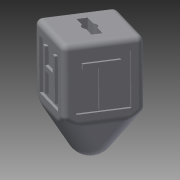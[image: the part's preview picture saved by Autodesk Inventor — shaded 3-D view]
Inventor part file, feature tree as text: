
AUTODESK INVENTOR PART (.ipt)
format: ipt  version: 2015 (Build 190159000, 159)  size: 379,904 bytes
history: native  units: in
note: dims shown in document units (in); Inventor stores cm internally (conversion verified against a paired STEP export)
features: extrude x13, sketch x13, projected_geometry x8, fillet x4
ambient origin geometry x8: Origin, YZ Plane, XZ Plane, XY Plane, X Axis, Y Axis, Z Axis, Center Point
bodies: Solid1 (feature_tree)
feature tree (38):
  extrude  "Extrusion1"  Depth=1.5in
  extrude  "Extrusion2"  Depth=0.25in
  extrude  "Extrusion3"  Depth=0.0625in
  fillet  "Fillet1"  Radius=0.4375in
  fillet  "Fillet2"  Radius=0.125in
  fillet  "Fillet3"  Radius=0.125in
  fillet  "Fillet4"  Radius=0.0625in
  extrude  "Extrusion4"  Depth=0.125in
  extrude  "Extrusion5"  Depth=0.125in
  extrude  "Extrusion6"  Depth=0.0625in TaperAngle=0.0deg
  extrude  "Extrusion7"  Depth=0.125in
  extrude  "Extrusion8"  Depth=0.125in
  extrude  "Extrusion9"  Depth=0.0625in TaperAngle=0.0deg
  extrude  "Extrusion10"  Depth=0.0625in TaperAngle=0.0deg
  extrude  "Extrusion11"  Depth=0.0625in TaperAngle=0.0deg
  extrude  "Extrusion12"  Depth=0.0625in TaperAngle=0.0deg
  extrude  "Extrusion13"  Depth=0.1in
  sketch  "Sketch1"  dims[d0=1.5in d1=1.5in]
  sketch  "Sketch2"  dims[d2=1.5in d3=0.0in d4=0.25in]
  sketch  "Sketch3"  dims[d5=1.25in d6=0.0in d7=1.3125in d8=-0.2061in d9=0.4375in d10=0.25in d11=0.125in d12=0.125in d13=0.0625in]
  projected_geometry  "Projected Loop1"
  sketch  "Sketch4"  dims[d14=0.125in d15=0.125in]
  projected_geometry  "Projected Loop2"
  sketch  "Sketch5"  dims[d16=0.125in d17=0.125in]
  projected_geometry  "Projected Loop3"
  sketch  "Sketch6"  dims[d18=0.125in d19=0.0625in d20=0.0in]
  projected_geometry  "Projected Loop4"
  sketch  "Sketch7"  dims[d21=0.0625in d22=0.0in d23=0.125in]
  projected_geometry  "Projected Loop5"
  sketch  "Sketch8"  dims[d24=0.125in d25=0.125in]
  projected_geometry  "Projected Loop6"
  sketch  "Sketch9"  dims[d26=0.125in d27=0.0625in d28=0.0in]
  projected_geometry  "Projected Loop7"
  sketch  "Sketch10"  dims[d29=0.0625in d30=0.0in d31=0.0625in d32=0.0in]
  sketch  "Sketch11"  dims[d33=0.0625in d34=0.0in d35=0.0625in d36=0.0in]
  projected_geometry  "Projected Loop8"
  sketch  "Sketch12"  dims[d37=0.0625in d38=0.0in d42=1.0in d43=0.0in]
  sketch  "Sketch13"  dims[d44=0.3in d47=0.1in d48=0.1in d49=0.4in d50=0.75in d51=0.0in]
